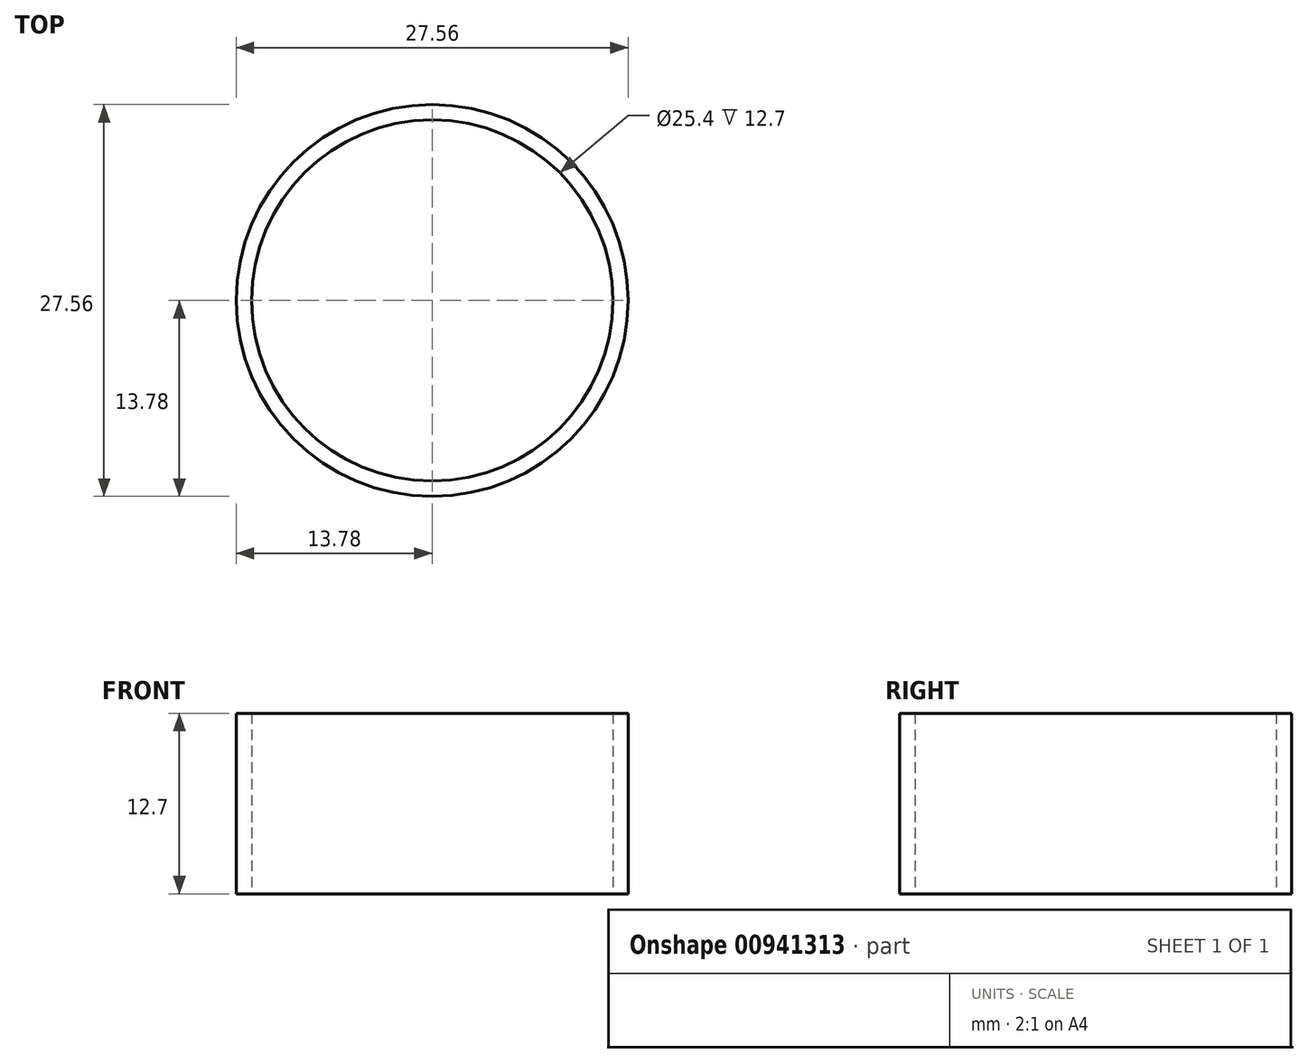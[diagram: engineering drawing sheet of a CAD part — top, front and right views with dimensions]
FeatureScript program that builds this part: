
annotation { "Feature Type Name" : "Feature", "Feature Type Description" : "" }
export const myFeature = defineFeature(function(context is Context, id is Id, definition is map)
    precondition{}
    {
        {
            var Q0;
            Q0=qCreatedBy(makeId("Top.planeOp"),FACE);
            var sketch = newSketch(context, id + "F0", { "sketchPlane" : qUnion([Q0])});
            skCircle(sketch, "E0", {"center": v(0, 0) * mm, "radius": 12.7 * mm});
            skCircle(sketch, "E1", {"center": v(0, 0) * mm, "radius": 13.78 * mm});
            skSolve(sketch);
        }
        {
            var Q0;
            Q0=makeQuery(id+"F0.imprint","IMPRINT",FACE,{"disambiguationData":[TD([[makeQuery(id+"F0.imprint","IMPRINT",EDGE,{"derivedFrom":sQuery(id+"F0.wireOp",EDGE,"E0")}),-1.0]])]});
            extrude(context, id + "F1", {"entities" : qUnion([Q0]), "depth" : 12.7 * mm, "offsetDistance" : 25.4 * mm});
        }
    });
